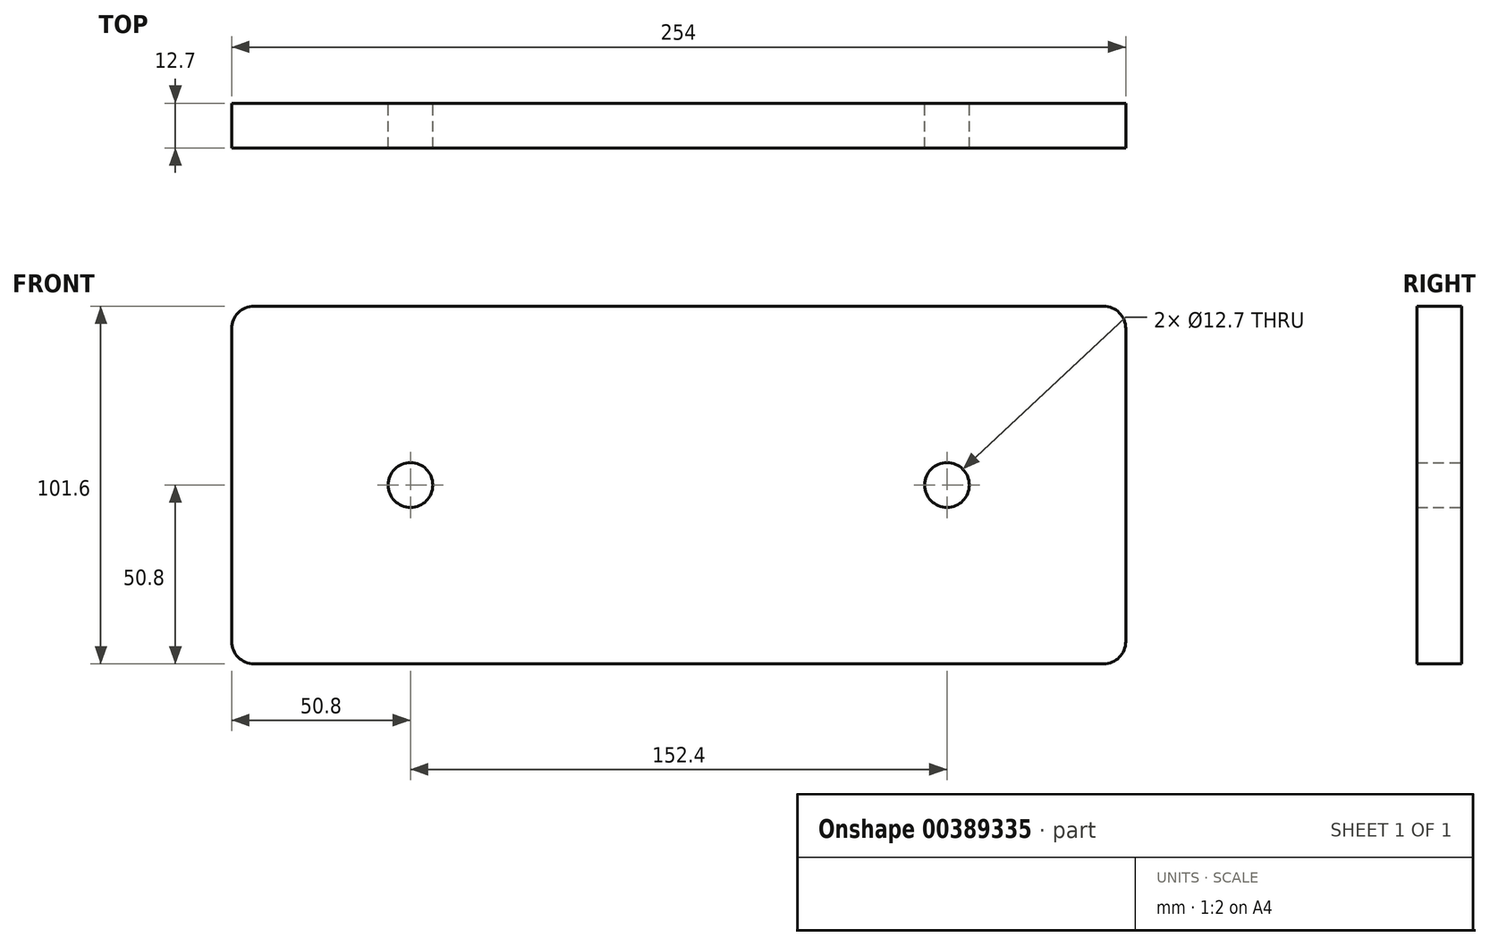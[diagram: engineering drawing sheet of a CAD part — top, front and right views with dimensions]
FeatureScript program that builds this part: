
annotation { "Feature Type Name" : "Feature", "Feature Type Description" : "" }
export const myFeature = defineFeature(function(context is Context, id is Id, definition is map)
    precondition{}
    {
        {
            var Q0;
            Q0=qCreatedBy(makeId("Front.planeOp"),FACE);
            var sketch = newSketch(context, id + "F0", { "sketchPlane" : qUnion([Q0])});
            skLineSegment(sketch, "E0.bottom", {"start": v(0, 0) * mm, "end": v(254, 0) * mm});
            skLineSegment(sketch, "E0.top", {"start": v(0, 101.6) * mm, "end": v(254, 101.6) * mm});
            skLineSegment(sketch, "E0.left", {"start": v(0, 0) * mm, "end": v(0, 101.6) * mm});
            skLineSegment(sketch, "E0.right", {"start": v(254, 0) * mm, "end": v(254, 101.6) * mm});
            skCircle(sketch, "E1", {"center": v(50.8, 50.8) * mm, "radius": 6.35 * mm});
            skCircle(sketch, "E2", {"center": v(203.2, 50.8) * mm, "radius": 6.35 * mm});
            skPoint(sketch, "E2.centerSnap0", {"position": v(254, 50.8) * mm});
            skSolve(sketch);
        }
        {
            var Q0;
            Q0 = qSketchRegion(id + "F0", true);
            extrude(context, id + "F1", {"entities" : qUnion([Q0]), "depth" : 12.7 * mm});
        }
        {
            var Q0;
            Q0=makeQuery(id+"F1.opExtrude","SWEPT_EDGE",EDGE,{"disambiguationData":[OSD([sQuery(id+"F0.wireOp",EDGE,"E0.top"),sQuery(id+"F0.wireOp",EDGE,"E0.left")])]});
            var Q1;
            Q1=makeQuery(id+"F1.opExtrude","SWEPT_EDGE",EDGE,{"disambiguationData":[OSD([sQuery(id+"F0.wireOp",EDGE,"E0.bottom"),sQuery(id+"F0.wireOp",EDGE,"E0.left")])]});
            var Q2;
            Q2=makeQuery(id+"F1.opExtrude","SWEPT_EDGE",EDGE,{"disambiguationData":[OSD([sQuery(id+"F0.wireOp",EDGE,"E0.bottom"),sQuery(id+"F0.wireOp",EDGE,"E0.right")])]});
            var Q3;
            Q3=makeQuery(id+"F1.opExtrude","SWEPT_EDGE",EDGE,{"disambiguationData":[OSD([sQuery(id+"F0.wireOp",EDGE,"E0.top"),sQuery(id+"F0.wireOp",EDGE,"E0.right")])]});
            fillet(context, id + "F2", {"entities" : qUnion([Q0, Q1, Q2, Q3]), "radius" : 6.35 * mm, "tangentPropagation" : true, "allowEdgeOverflow" : false});
        }
    });
